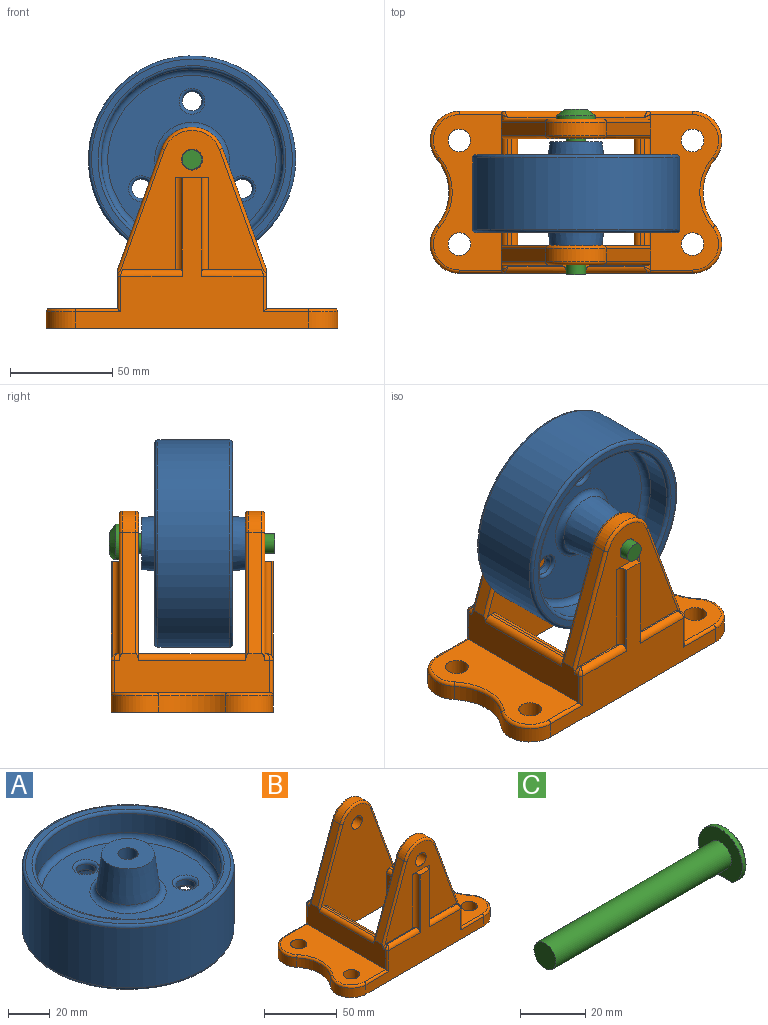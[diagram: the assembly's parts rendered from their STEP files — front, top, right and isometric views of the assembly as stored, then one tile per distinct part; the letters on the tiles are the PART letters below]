
ASSEMBLY  parts=3 mates=2
PART A: 29 faces, bbox 110x110x50.8 mm
  f0: cylinder r=4.83mm len=50.8mm, axis (0,0,-1), area 1540.4mm2, adj f10,f13
  f1: cylinder r=44.45mm len=88.9mm, axis (0,0,1), area 3103.6mm2, adj f16,f22
  f2: cylinder r=44.45mm len=88.9mm, axis (0,0,-1), area 3103.6mm2, adj f18,f27
  f3: cylinder r=50.8mm len=101.6mm, axis (0,0,-1), area 11147.6mm2, adj f23,f28
  f4: plane 98.43x98.43mm, normal (0,0,1), area 950.1mm2, adj f27,f28
  f5: cylinder r=4.76mm len=9.53mm, axis (0,0,-1), area 95mm2, adj f21,f26
  f6: cylinder r=4.76mm len=9.53mm, axis (0,0,-1), area 95mm2, adj f20,f25
  f7: cylinder r=4.76mm len=9.53mm, axis (0,0,-1), area 95mm2, adj f19,f24
  f8: plane 82.55x82.55mm, normal (0,0,1), area 3922.2mm2, adj f17,f18,f24,f25,f26
  f9: cone r=15.88mm half-angle=7.1deg, axis (0,0,-1), area 1713.2mm2, adj f10,f17
  f10: plane 25.4x25.4mm, normal (0,0,1), area 433.5mm2, adj f0,f9
  f11: plane 98.43x98.43mm, normal (0,0,-1), area 950.1mm2, adj f22,f23
  f12: plane 82.55x82.55mm, normal (0,0,-1), area 3922.2mm2, adj f15,f16,f19,f20,f21
  f13: plane 25.4x25.4mm, normal (0,0,-1), area 433.5mm2, adj f0,f14
  f14: cone r=12.7mm half-angle=7.1deg, axis (0,0,1), area 1713.2mm2, adj f13,f15
  f15: torus R=18.28mm, axis (0,0,1), area 472mm2, adj f12,f14
  f16: torus R=41.27mm, axis (0,0,1), area 1356.7mm2, adj f1,f12
  f17: torus R=18.28mm, axis (0,0,1), area 472mm2, adj f8,f9
  f18: torus R=41.27mm, axis (0,0,1), area 1356.7mm2, adj f2,f8
  f19: torus R=6.35mm, axis (0,0,1), area 83.7mm2, adj f7,f12
  f20: torus R=6.35mm, axis (0,0,1), area 83.7mm2, adj f6,f12
  f21: torus R=6.35mm, axis (0,0,1), area 83.7mm2, adj f5,f12
  f22: torus R=46.04mm, axis (0,0,1), area 705.5mm2, adj f1,f11
  f23: torus R=49.21mm, axis (0,0,1), area 786.9mm2, adj f3,f11
  f24: torus R=6.35mm, axis (0,0,1), area 83.7mm2, adj f7,f8
  f25: torus R=6.35mm, axis (0,0,1), area 83.7mm2, adj f6,f8
  f26: torus R=6.35mm, axis (0,0,1), area 83.7mm2, adj f5,f8
  f27: torus R=46.04mm, axis (0,0,1), area 705.5mm2, adj f2,f4
  f28: torus R=49.21mm, axis (0,0,1), area 786.9mm2, adj f3,f4
PART B: 89 faces, bbox 145.2x81.7x99.7 mm
  f0: plane 96.84x69.99mm, normal (0,-1,0), area 4577.3mm2, adj f4,f8,f11,f12,f26,f41,f73,f74
  f1: plane 96.84x69.99mm, normal (0,1,0), area 4577.3mm2, adj f4,f8,f11,f12,f26,f40,f73,f74
  f2: plane 69.99x68.73mm, normal (0,1,0), area 2222.4mm2, adj f7,f9,f34,f41,f59,f60,f63,f69
  f3: plane 69.99x68.73mm, normal (0,-1,0), area 2222.4mm2, adj f5,f6,f31,f40,f57,f58,f66,f72
  f4: plane 52.39x1.6mm, normal (0,0,1), area 83.8mm2, adj f0,f1,f73,f75
  f5: plane 27.5x0.79mm, normal (0,0,1), area 21.3mm2, adj f3,f57,f64,f66
  f6: plane 27.5x0.79mm, normal (0,0,1), area 21.3mm2, adj f3,f58,f70,f72
  f7: plane 27.5x0.79mm, normal (0,0,1), area 21.3mm2, adj f2,f59,f61,f63
  f8: plane 52.39x1.6mm, normal (0,0,1), area 83.8mm2, adj f0,f1,f74,f76
  f9: plane 27.5x0.79mm, normal (0,0,1), area 21.3mm2, adj f2,f60,f67,f69
  f10: plane 76.2x33.34mm, normal (0,0,1), area 2012.7mm2, adj f21,f22,f28,f44,f45,f46,f48,f49
  f11: plane 52.39x25.4mm, normal (1,0,0), area 1330.6mm2, adj f0,f1,f26,f76
  f12: plane 52.39x25.4mm, normal (-1,0,0), area 1330.6mm2, adj f0,f1,f26,f75
  f13: plane 114.3x73.82mm, normal (0,-1,0), area 2588.2mm2, adj f14,f23,f26,f29,f30,f31,f47,f49
  f14: cylinder r=14.29mm len=23.43mm, axis (0,0,-1), area 256.9mm2, adj f13,f15,f26,f54
  f15: cylinder r=25.4mm len=32.51mm, axis (0,0,-1), area 280mm2, adj f14,f16,f26,f53
  f16: cylinder r=14.29mm len=23.43mm, axis (0,0,-1), area 256.9mm2, adj f15,f17,f26,f52
  f17: plane 114.3x73.82mm, normal (0,1,0), area 2588.2mm2, adj f16,f18,f26,f32,f33,f34,f43,f44
  f18: cylinder r=14.29mm len=23.43mm, axis (0,0,-1), area 256.9mm2, adj f17,f19,f26,f45
  f19: cylinder r=25.4mm len=32.51mm, axis (0,0,-1), area 280mm2, adj f18,f23,f26,f46
  f20: cylinder r=5.56mm len=11.11mm, axis (0,0,-1), area 332.5mm2, adj f25,f26
  f21: cylinder r=5.56mm len=11.11mm, axis (0,0,-1), area 332.5mm2, adj f10,f26
  f22: cylinder r=5.56mm len=11.11mm, axis (0,0,-1), area 332.5mm2, adj f10,f26
  f23: cylinder r=14.29mm len=23.43mm, axis (0,0,-1), area 256.9mm2, adj f13,f19,f26,f48
  f24: cylinder r=5.56mm len=11.11mm, axis (0,0,-1), area 332.5mm2, adj f25,f26
  f25: plane 76.2x33.34mm, normal (0,0,1), area 2012.7mm2, adj f20,f24,f27,f51,f52,f53,f54,f56
  f26: plane 142.88x79.38mm, normal (0,0,-1), area 7269.9mm2, adj f0,f1,f11,f12,f13,f14,f15,f16
  f27: plane 76.2x19.05mm, normal (1,0,0), area 1264mm2, adj f25,f36,f37,f50,f55,f63,f66,f73
  f28: plane 76.2x19.05mm, normal (-1,0,0), area 1264mm2, adj f10,f39,f42,f43,f47,f69,f72,f74
  f29: plane 48.42x0.79mm, normal (1,0,0), area 37.3mm2, adj f13,f31,f57,f64
  f30: plane 48.42x0.79mm, normal (-1,0,0), area 37.3mm2, adj f13,f31,f58,f70
  f31: plane 15.88x3.97mm, normal (0,0,1), area 42.1mm2, adj f3,f13,f29,f30,f57,f58
  f32: plane 48.42x0.79mm, normal (-1,0,0), area 37.3mm2, adj f17,f34,f60,f67
  f33: plane 48.42x0.79mm, normal (1,0,0), area 37.3mm2, adj f17,f34,f59,f61
  f34: plane 15.88x3.97mm, normal (0,0,1), area 42.1mm2, adj f2,f17,f32,f33,f59,f60
  f35: cylinder r=15.88mm len=29.84mm, axis (0,1,0), area 246.4mm2, adj f36,f39,f81,f84
  f36: plane 59.4x21.59mm, normal (0.94,0,0.34), area 401.3mm2, adj f27,f35,f80,f83
  f37: plane 59.4x21.59mm, normal (0.94,0,0.34), area 401.3mm2, adj f27,f38,f77,f86
  f38: cylinder r=15.88mm len=29.84mm, axis (0,1,0), area 246.4mm2, adj f37,f42,f78,f87
  f39: plane 59.4x21.59mm, normal (-0.94,0,0.34), area 401.3mm2, adj f28,f35,f82,f85
  f40: cylinder r=5.16mm len=10.32mm, axis (0,1,0), area 308.8mm2, adj f1,f3
  f41: cylinder r=5.16mm len=10.32mm, axis (0,1,0), area 308.8mm2, adj f0,f2
  f42: plane 59.4x21.59mm, normal (-0.94,0,0.34), area 401.3mm2, adj f28,f38,f79,f88
  f43: cylinder r=1.59mm len=17.46mm, axis (0,0,-1), area 41mm2, adj f17,f28,f44,f68
  f44: cylinder r=1.59mm len=22.23mm, axis (1,0,0), area 52.9mm2, adj f10,f17,f43,f45
  f45: torus R=12.7mm, axis (0,0,1), area 77.4mm2, adj f10,f18,f44,f46
  f46: torus R=26.99mm, axis (0,0,1), area 90mm2, adj f10,f19,f45,f48
  f47: cylinder r=1.59mm len=17.46mm, axis (0,0,1), area 41mm2, adj f13,f28,f49,f71
  f48: torus R=12.7mm, axis (0,0,1), area 77.4mm2, adj f10,f23,f46,f49
  f49: cylinder r=1.59mm len=22.23mm, axis (-1,0,0), area 52.9mm2, adj f10,f13,f47,f48
  f50: cylinder r=1.59mm len=17.46mm, axis (0,0,1), area 41mm2, adj f17,f27,f51,f62
  f51: cylinder r=1.59mm len=22.23mm, axis (1,0,0), area 52.9mm2, adj f17,f25,f50,f52
  f52: torus R=12.7mm, axis (0,0,1), area 77.4mm2, adj f16,f25,f51,f53
  f53: torus R=26.99mm, axis (0,0,1), area 90mm2, adj f15,f25,f52,f54
  f54: torus R=12.7mm, axis (0,0,1), area 77.4mm2, adj f14,f25,f53,f56
  f55: cylinder r=1.59mm len=17.46mm, axis (0,0,-1), area 41mm2, adj f13,f27,f56,f65
  f56: cylinder r=1.59mm len=22.23mm, axis (-1,0,0), area 52.9mm2, adj f13,f25,f54,f55
  f57: cylinder r=3.17mm len=46.32mm, axis (0,0,1), area 226.5mm2, adj f3,f5,f29,f31,f64
  f58: cylinder r=3.17mm len=46.32mm, axis (0,0,-1), area 226.5mm2, adj f3,f6,f30,f31,f70
  f59: cylinder r=3.17mm len=46.32mm, axis (0,0,1), area 226.5mm2, adj f2,f7,f33,f34,f61
  f60: cylinder r=3.17mm len=46.32mm, axis (0,0,-1), area 226.5mm2, adj f2,f9,f32,f34,f67
  f61: cylinder r=3.17mm len=30.16mm, axis (1,0,0), area 146.7mm2, adj f7,f17,f33,f59,f62
  f62: bspline ~3.79x3.18mm, area 8.3mm2, adj f50,f61,f63
  f63: cylinder r=3.17mm len=3.18mm, axis (0,-1,0), area 9.3mm2, adj f2,f7,f27,f62,f86
  f64: cylinder r=3.17mm len=30.16mm, axis (-1,0,0), area 146.7mm2, adj f5,f13,f29,f57,f65
  f65: bspline ~3.79x3.18mm, area 8.3mm2, adj f55,f64,f66
  f66: cylinder r=3.17mm len=3.18mm, axis (0,-1,0), area 9.3mm2, adj f3,f5,f27,f65,f83
  f67: cylinder r=3.17mm len=30.16mm, axis (1,0,0), area 146.7mm2, adj f9,f17,f32,f60,f68
  f68: bspline ~3.79x3.18mm, area 8.3mm2, adj f43,f67,f69
  f69: cylinder r=3.17mm len=3.18mm, axis (0,1,0), area 9.3mm2, adj f2,f9,f28,f68,f88
  f70: cylinder r=3.17mm len=30.16mm, axis (-1,0,0), area 146.7mm2, adj f6,f13,f30,f58,f71
  f71: bspline ~3.79x3.18mm, area 8.3mm2, adj f47,f70,f72
  f72: cylinder r=3.17mm len=3.18mm, axis (0,1,0), area 9.3mm2, adj f3,f6,f28,f71,f85
  f73: cylinder r=3.17mm len=52.71mm, axis (0,-1,0), area 261.9mm2, adj f0,f1,f4,f27,f77,f80
  f74: cylinder r=3.17mm len=52.71mm, axis (0,1,0), area 261.9mm2, adj f0,f1,f8,f28,f79,f82
  f75: cylinder r=3.17mm len=52.39mm, axis (0,1,0), area 261.3mm2, adj f0,f1,f4,f12
  f76: cylinder r=3.17mm len=52.39mm, axis (0,-1,0), area 261.3mm2, adj f0,f1,f8,f11
  f77: cylinder r=1.59mm len=62.75mm, axis (-0.34,0,0.94), area 159.5mm2, adj f0,f27,f37,f73,f78
  f78: torus R=14.29mm, axis (0,1,0), area 93.2mm2, adj f0,f38,f77,f79
  f79: cylinder r=1.59mm len=62.75mm, axis (-0.34,0,-0.94), area 159.5mm2, adj f0,f28,f42,f74,f78
  f80: cylinder r=1.59mm len=62.75mm, axis (0.34,0,-0.94), area 159.5mm2, adj f1,f27,f36,f73,f81
  f81: torus R=14.29mm, axis (0,1,0), area 93.2mm2, adj f1,f35,f80,f82
  f82: cylinder r=1.59mm len=62.75mm, axis (0.34,0,0.94), area 159.5mm2, adj f1,f28,f39,f74,f81
  f83: cylinder r=1.59mm len=62.75mm, axis (-0.34,0,0.94), area 159.5mm2, adj f3,f27,f36,f66,f84
  f84: torus R=14.29mm, axis (0,1,0), area 93.2mm2, adj f3,f35,f83,f85
  f85: cylinder r=1.59mm len=62.75mm, axis (-0.34,0,-0.94), area 159.5mm2, adj f3,f28,f39,f72,f84
  f86: cylinder r=1.59mm len=62.75mm, axis (0.34,0,-0.94), area 159.5mm2, adj f2,f27,f37,f63,f87
  f87: torus R=14.29mm, axis (0,1,0), area 93.2mm2, adj f2,f38,f86,f88
  f88: cylinder r=1.59mm len=62.75mm, axis (0.34,0,0.94), area 159.5mm2, adj f2,f28,f42,f69,f87
PART C: 7 faces, bbox 81x19.1x19.1 mm
  f0: cylinder r=4.76mm len=76.2mm, axis (1,0,0), area 2280.2mm2, adj f1,f5
  f1: plane 19.05x17.46mm, normal (-1,0,0), area 202.4mm2, adj f0,f2,f6
  f2: cylinder r=9.53mm len=19.05mm, axis (1,0,0), area 77.3mm2, adj f1,f3,f6
  f3: cone r=5.56mm half-angle=51.2deg, axis (-1,0,0), area 226.6mm2, adj f2,f4,f6
  f4: plane 11.11x11.11mm, normal (1,0,0), area 97mm2, adj f3
  f5: plane 9.53x9.53mm, normal (-1,0,0), area 71.3mm2, adj f0
  f6: plane 10.54x2.87mm, normal (0,0,-1), area 25.5mm2, adj f1,f2,f3
PLACE A rot(axis=(1,0,0),90deg) t=(-93.26,-21.59,28.42)mm
PLACE B t=(-93.26,-20.8,-54.13)mm
PLACE C rot(axis=(0,0,1),90deg) t=(-90.88,-23.18,28.42)mm
MATE revolute A.f9 <-> C.f0  axis (0,-1,0) through (-93.26,-46.99,28.42)mm
MATE fastened C.f0 <-> B.f40  axis (0,-1,0) through (-93.26,14.92,28.42)mm
